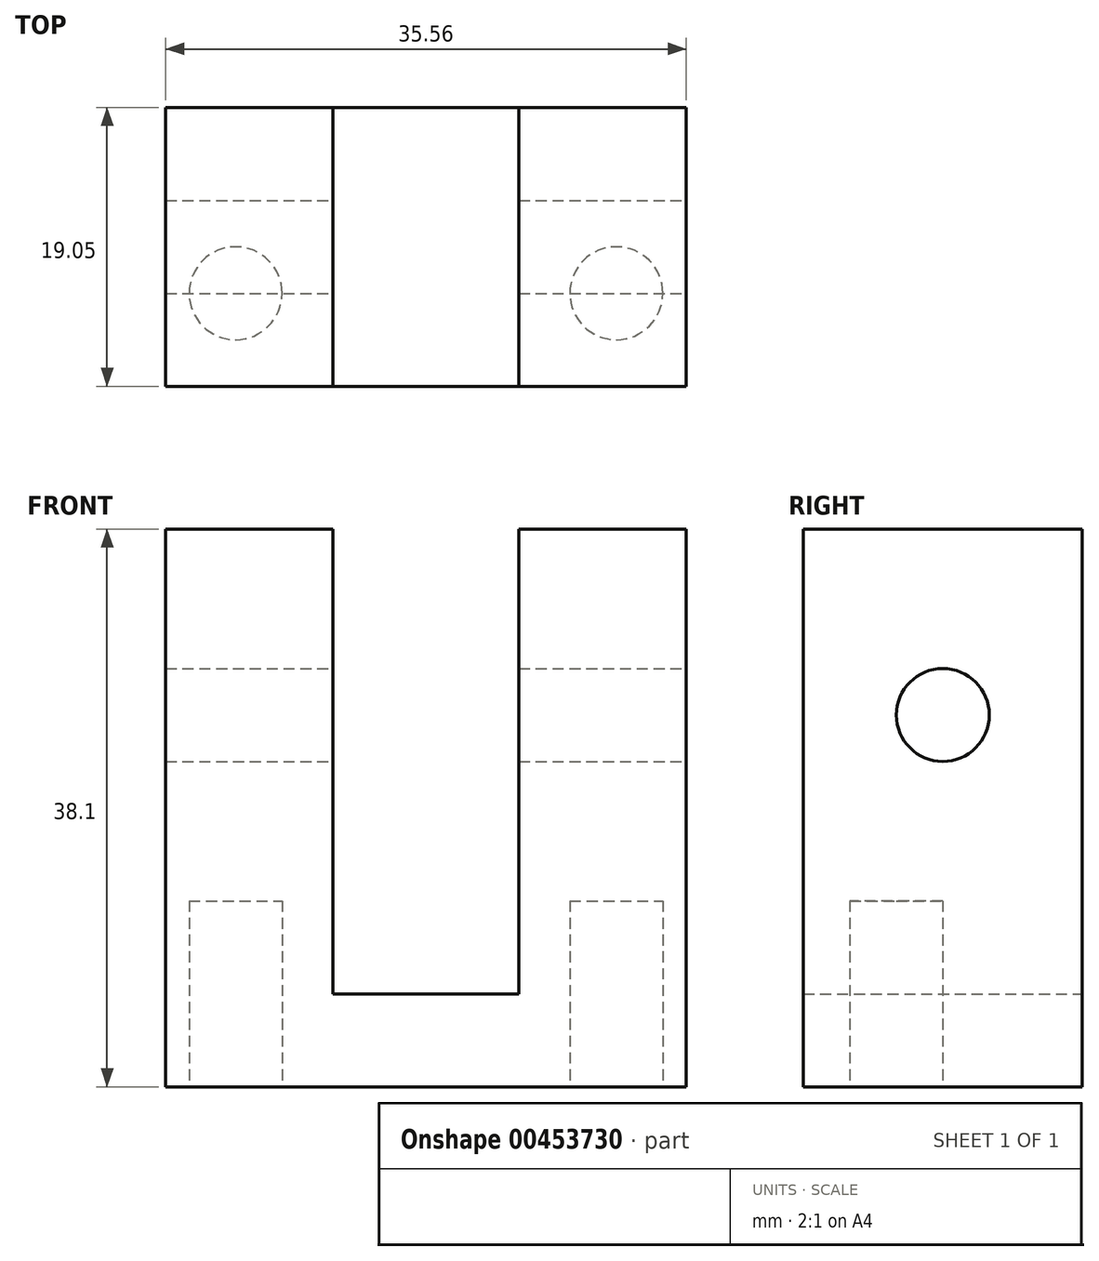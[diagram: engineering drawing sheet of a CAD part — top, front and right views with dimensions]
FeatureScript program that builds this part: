
annotation { "Feature Type Name" : "Feature", "Feature Type Description" : "" }
export const myFeature = defineFeature(function(context is Context, id is Id, definition is map)
    precondition{}
    {
        {
            var Q0;
            Q0=qCreatedBy(makeId("Front.planeOp"),FACE);
            var sketch = newSketch(context, id + "F0", { "sketchPlane" : qUnion([Q0])});
            skLineSegment(sketch, "E0.bottom", {"start": v(-17.78, 18.69) * mm, "end": v(-6.35, 18.69) * mm});
            skLineSegment(sketch, "E0.top", {"start": v(-17.78, -19.41) * mm, "end": v(17.78, -19.41) * mm});
            skLineSegment(sketch, "E0.left", {"start": v(-17.78, 18.69) * mm, "end": v(-17.78, -19.41) * mm});
            skLineSegment(sketch, "E0.right", {"start": v(17.78, 18.69) * mm, "end": v(17.78, -19.41) * mm});
            skLineSegment(sketch, "E1", {"start": v(-6.35, 18.69) * mm, "end": v(-6.35, -13.06) * mm});
            skLineSegment(sketch, "E2", {"start": v(-6.35, -13.06) * mm, "end": v(6.35, -13.06) * mm});
            skLineSegment(sketch, "E3", {"start": v(6.35, -13.06) * mm, "end": v(6.35, 18.69) * mm});
            skLineSegment(sketch, "E4.trimOffspring", {"start": v(6.35, 18.69) * mm, "end": v(17.78, 18.69) * mm});
            skSolve(sketch);
        }
        {
            var Q0;
            Q0=makeQuery(id+"F0.imprint","IMPRINT",FACE,{"disambiguationData":[TD([[makeQuery(id+"F0.imprint","IMPRINT",EDGE,{"derivedFrom":sQuery(id+"F0.wireOp",EDGE,"E0.bottom")}),-1.0]])]});
            extrude(context, id + "F1", {"entities" : qUnion([Q0]), "depth" : 19.05 * mm});
        }
        {
            var Q0;
            Q0=makeQuery(id+"F1.opExtrude","SWEPT_FACE",FACE,{"disambiguationData":[OSD([sQuery(id+"F0.wireOp",EDGE,"E0.right")])]});
            var sketch = newSketch(context, id + "F2", { "sketchPlane" : qUnion([Q0])});
            skCircle(sketch, "E5", {"center": v(-9.53, 5.99) * mm, "radius": 3.18 * mm});
            skSolve(sketch);
        }
        {
            var Q0;
            Q0=makeQuery(id+"F2.imprint","IMPRINT",FACE,{"disambiguationData":[TD([[makeQuery(id+"F2.imprint","IMPRINT",EDGE,{"derivedFrom":sQuery(id+"F2.wireOp",EDGE,"E5")}),1.0]])]});
            extrude(context, id + "F3", {"entities" : qUnion([Q0]), "operationType" : NewBodyOperationType.REMOVE, "endBound" : BoundingType.THROUGH_ALL, "oppositeDirection" : true, "depth" : 25.4 * mm});
        }
        {
            var Q0;
            Q0=makeQuery(id+"F1.opExtrude","SWEPT_FACE",FACE,{"disambiguationData":[OSD([sQuery(id+"F0.wireOp",EDGE,"E0.top")])]});
            var sketch = newSketch(context, id + "F4", { "sketchPlane" : qUnion([Q0])});
            skCircle(sketch, "E6", {"center": v(-13, 12.7) * mm, "radius": 3.18 * mm});
            skCircle(sketch, "E7", {"center": v(13, 12.7) * mm, "radius": 3.18 * mm});
            skSolve(sketch);
        }
        {
            var Q0;
            Q0=makeQuery(id+"F4.imprint","IMPRINT",FACE,{"disambiguationData":[TD([[makeQuery(id+"F4.imprint","IMPRINT",EDGE,{"derivedFrom":sQuery(id+"F4.wireOp",EDGE,"E6")}),1.0]])]});
            var Q1;
            Q1=makeQuery(id+"F4.imprint","IMPRINT",FACE,{"disambiguationData":[TD([[makeQuery(id+"F4.imprint","IMPRINT",EDGE,{"derivedFrom":sQuery(id+"F4.wireOp",EDGE,"E7")}),1.0]])]});
            extrude(context, id + "F5", {"entities" : qUnion([Q0, Q1]), "operationType" : NewBodyOperationType.REMOVE, "oppositeDirection" : true, "depth" : 12.7 * mm});
        }
    });
